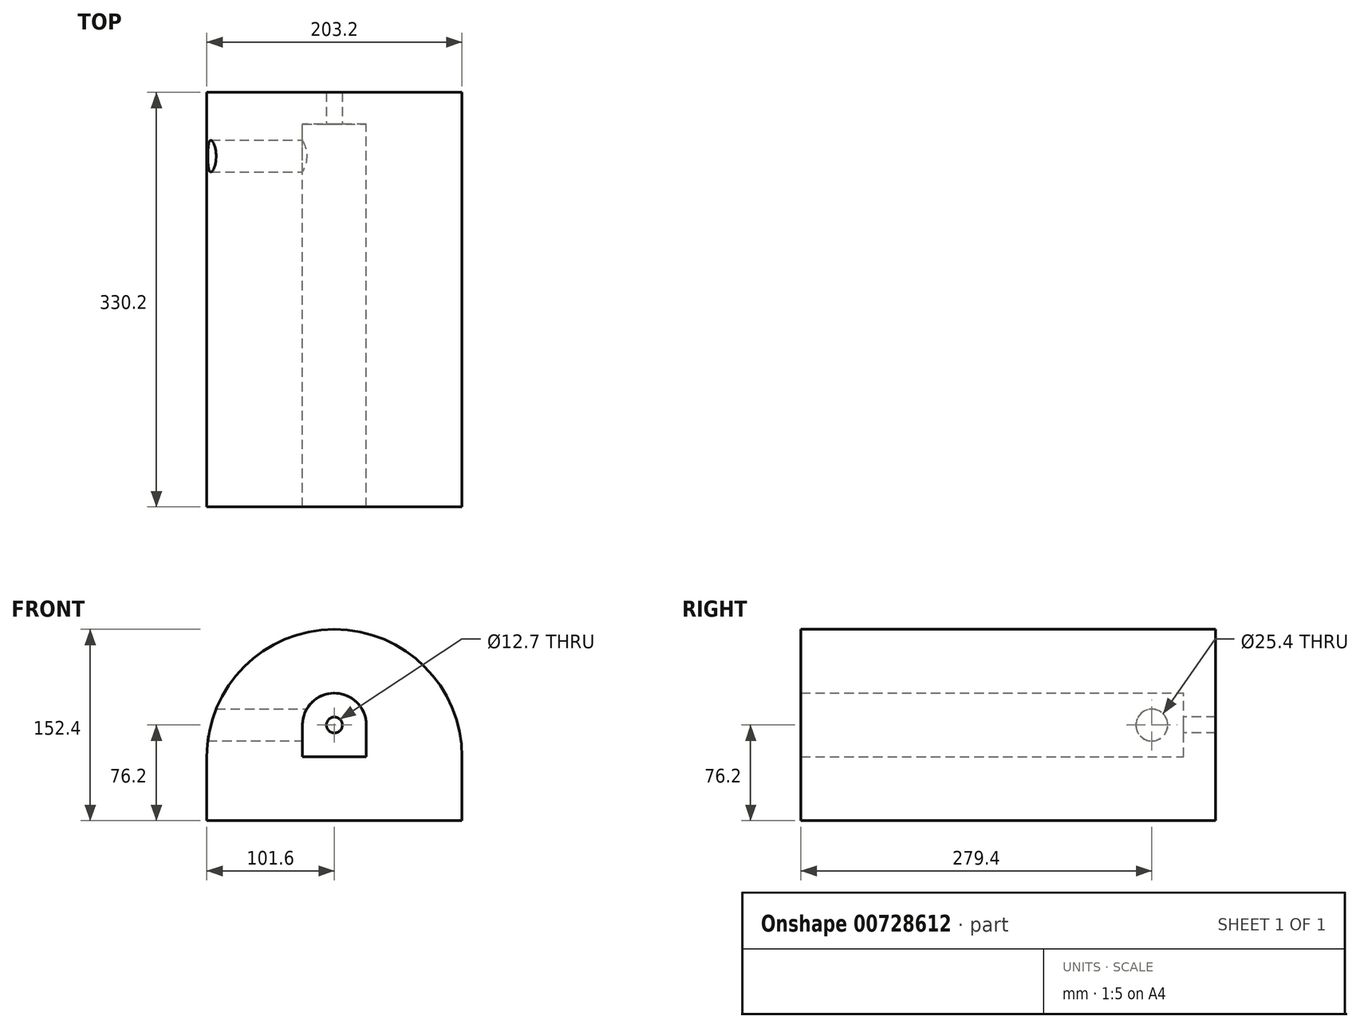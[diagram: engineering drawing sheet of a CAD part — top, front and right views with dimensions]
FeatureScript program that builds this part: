
annotation { "Feature Type Name" : "Feature", "Feature Type Description" : "" }
export const myFeature = defineFeature(function(context is Context, id is Id, definition is map)
    precondition{}
    {
        {
            var Q0;
            Q0=qCreatedBy(makeId("Front.planeOp"),FACE);
            var sketch = newSketch(context, id + "F0", { "sketchPlane" : qUnion([Q0])});
            skArc(sketch, "E0", {"start": v(25.4, 25.4) * mm, "mid": v(0, 50.8) * mm, "end": v(-25.4, 25.4) * mm});
            skLineSegment(sketch, "E1", {"start": v(-25.4, 25.4) * mm, "end": v(-25.4, 0) * mm});
            skLineSegment(sketch, "E2", {"start": v(-25.4, 0) * mm, "end": v(25.4, 0) * mm});
            skLineSegment(sketch, "E3", {"start": v(25.4, 0) * mm, "end": v(25.4, 25.4) * mm});
            skArc(sketch, "E4", {"start": v(101.6, 0) * mm, "mid": v(0, 101.6) * mm, "end": v(-101.6, 0) * mm});
            skLineSegment(sketch, "E5", {"start": v(0, 0) * mm, "end": v(-101.6, 0) * mm});
            skLineSegment(sketch, "E6", {"start": v(0, 0) * mm, "end": v(101.6, 0) * mm});
            skLineSegment(sketch, "E7", {"start": v(-101.6, 0) * mm, "end": v(-101.6, -50.8) * mm});
            skLineSegment(sketch, "E8", {"start": v(101.6, 0) * mm, "end": v(101.6, -50.8) * mm});
            skLineSegment(sketch, "E9", {"start": v(101.6, -50.8) * mm, "end": v(-101.6, -50.8) * mm});
            skSolve(sketch);
        }
        {
            var Q0;
            Q0=makeQuery(id+"F0.imprint","IMPRINT",FACE,{"disambiguationData":[TD([[makeQuery(id+"F0.imprint","IMPRINT",EDGE,{"derivedFrom":sQuery(id+"F0.wireOp",EDGE,"E0")}),-1.0]])]});
            var Q1;
            {var subQ7=sQuery(id+"F0.wireOp",EDGE,"E7");Q1=makeQuery(id+"F0.imprint","IMPRINT",FACE,{"disambiguationData":[TD([[makeQuery(id+"F0.imprint","IMPRINT",EDGE,{"derivedFrom":subQ7}),1.0]])]});}
            extrude(context, id + "F1", {"entities" : qUnion([Q0, Q1]), "depth" : 304.8 * mm, "offsetDistance" : 25.4 * mm});
        }
        {
            var Q0;
            Q0=makeQuery(id+"F1.opExtrude","CAP_FACE",FACE,{"disambiguationData":[OSD([sQuery(id+"F0.wireOp",EDGE,"E0"),sQuery(id+"F0.wireOp",EDGE,"E1"),sQuery(id+"F0.wireOp",EDGE,"E3"),sQuery(id+"F0.wireOp",EDGE,"E4"),sQuery(id+"F0.wireOp",EDGE,"E5"),sQuery(id+"F0.wireOp",EDGE,"E6"),sQuery(id+"F0.wireOp",EDGE,"E7"),sQuery(id+"F0.wireOp",EDGE,"E8"),sQuery(id+"F0.wireOp",EDGE,"E9")])],"isStart":true});
            var sketch = newSketch(context, id + "F2", { "sketchPlane" : qUnion([Q0])});
            skArc(sketch, "E10", {"start": v(101.6, 0) * mm, "mid": v(0, 101.6) * mm, "end": v(-101.6, 0) * mm});
            skLineSegment(sketch, "E11", {"start": v(-101.6, 0) * mm, "end": v(-101.6, -50.8) * mm});
            skLineSegment(sketch, "E12", {"start": v(-101.6, -50.8) * mm, "end": v(101.6, -50.8) * mm});
            skLineSegment(sketch, "E13", {"start": v(101.6, -50.8) * mm, "end": v(101.6, 0) * mm});
            skSolve(sketch);
        }
        {
            var Q0;
            Q0 = qSketchRegion(id + "F2", true);
            extrude(context, id + "F3", {"entities" : qUnion([Q0]), "operationType" : NewBodyOperationType.ADD, "depth" : 25.4 * mm, "offsetDistance" : 25.4 * mm});
        }
        {
            var Q0;
            Q0=qCreatedBy(makeId("Front.planeOp"),FACE);
            var sketch = newSketch(context, id + "F4", { "sketchPlane" : qUnion([Q0])});
            skCircle(sketch, "E14", {"center": v(0, 25.4) * mm, "radius": 6.35 * mm});
            skSolve(sketch);
        }
        {
            var Q0;
            Q0=makeQuery(id+"F4.imprint","IMPRINT",FACE,{"disambiguationData":[TD([[makeQuery(id+"F4.imprint","IMPRINT",EDGE,{"derivedFrom":sQuery(id+"F4.wireOp",EDGE,"E14")}),1.0]])]});
            extrude(context, id + "F5", {"entities" : qUnion([Q0]), "operationType" : NewBodyOperationType.REMOVE, "endBound" : BoundingType.THROUGH_ALL, "oppositeDirection" : true, "depth" : 25.4 * mm, "offsetDistance" : 25.4 * mm});
        }
        {
            var Q0;
            Q0=qCreatedBy(makeId("Right.planeOp"),FACE);
            var sketch = newSketch(context, id + "F6", { "sketchPlane" : qUnion([Q0])});
            skLineSegment(sketch, "E15", {"start": v(0, 0) * mm, "end": v(0, 25.4) * mm});
            skLineSegment(sketch, "E16", {"start": v(0, 25.4) * mm, "end": v(-25.4, 25.4) * mm});
            skCircle(sketch, "E17", {"center": v(-25.4, 25.4) * mm, "radius": 12.7 * mm});
            skSolve(sketch);
        }
        {
            var Q0;
            Q0=makeQuery(id+"F6.imprint","IMPRINT",FACE,{"disambiguationData":[TD([[makeQuery(id+"F6.imprint","IMPRINT",EDGE,{"derivedFrom":sQuery(id+"F6.wireOp",EDGE,"E17")}),1.0]])]});
            extrude(context, id + "F7", {"entities" : qUnion([Q0]), "operationType" : NewBodyOperationType.REMOVE, "endBound" : BoundingType.THROUGH_ALL, "oppositeDirection" : true, "depth" : 25.4 * mm, "offsetDistance" : 25.4 * mm});
        }
    });
